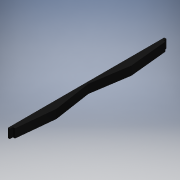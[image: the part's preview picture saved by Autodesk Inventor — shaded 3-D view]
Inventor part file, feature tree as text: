
AUTODESK INVENTOR PART (.ipt)
format: ipt  version: 2017 (Build 210142000, 142)  size: 120,832 bytes
history: native  units: in
note: dims shown in document units (in); Inventor stores cm internally (conversion verified against a paired STEP export)
features: extrude x3, sketch x3
ambient origin geometry x8: Origin, YZ Plane, XZ Plane, XY Plane, X Axis, Y Axis, Z Axis, Center Point
bodies: Solid1 (feature_tree)
feature tree (6):
  extrude  "Extrusion1"  Depth=0.134in
  sketch  "Sketch2"  dims[d2=0.134in d3=1.2353in]
  sketch  "Sketch3"  dims[d4=2.4705in d5=1.2353in d6=0.125in d7=0.125in d8=0.2875in d9=0.0in d10=0.065in d11=0.065in d12=0.101in d13=0.0in d14=0.101in d15=0.0in]
  extrude  "Extrusion2"  Depth=0.134in
  extrude  "Extrusion3"  Depth=0.101in
  sketch  "Sketch1"  dims[d0=4.931in d1=0.134in]
